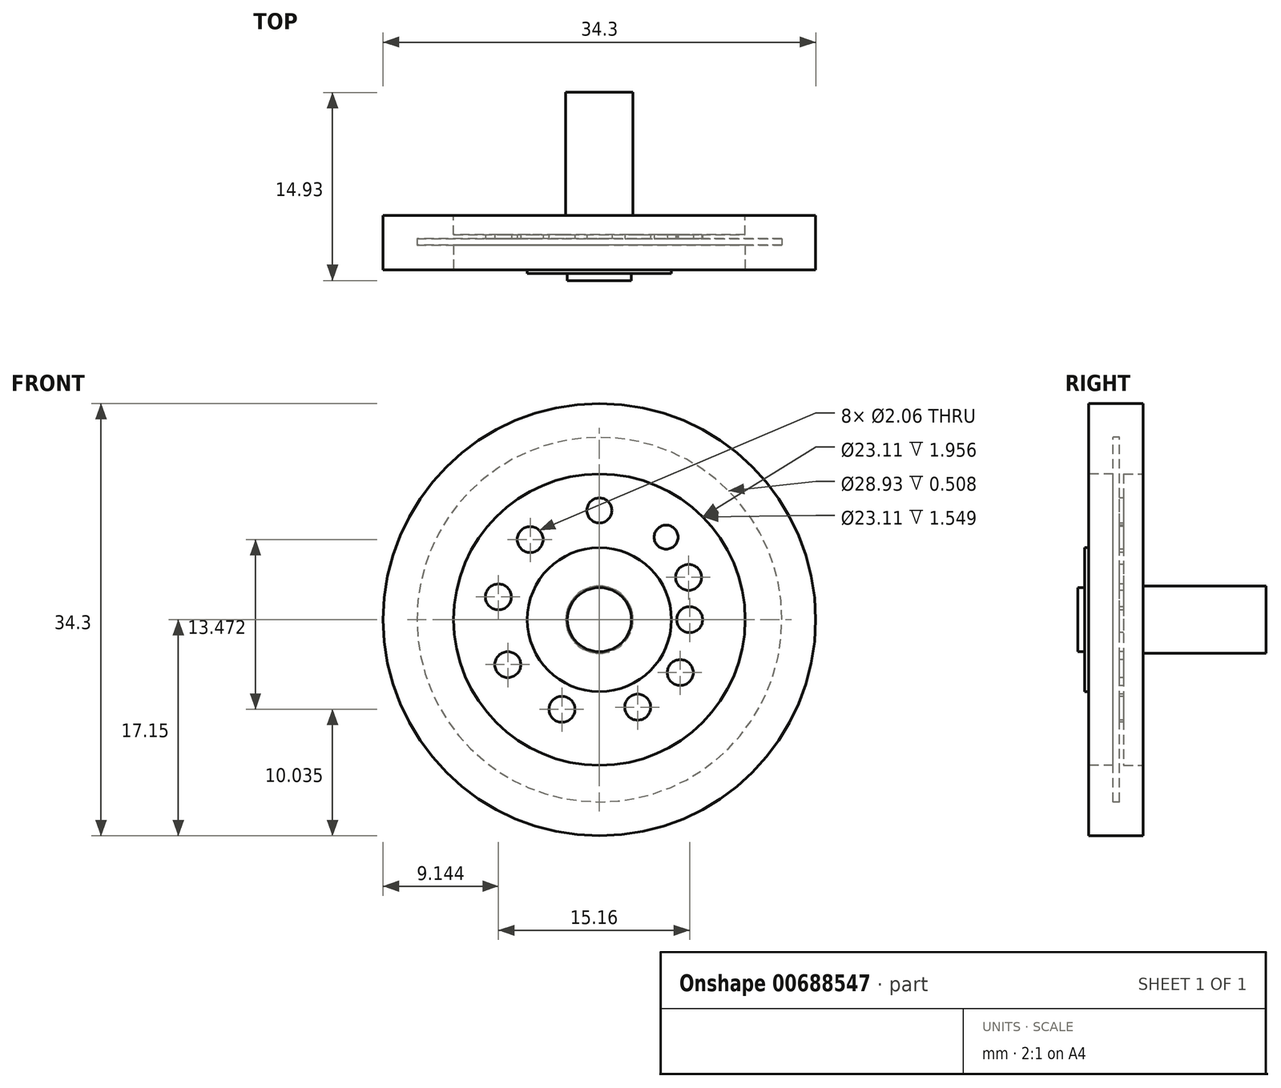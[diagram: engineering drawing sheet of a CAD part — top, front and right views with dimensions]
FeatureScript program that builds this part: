
annotation { "Feature Type Name" : "Feature", "Feature Type Description" : "" }
export const myFeature = defineFeature(function(context is Context, id is Id, definition is map)
    precondition{}
    {
        {
            var Q0;
            Q0=qCreatedBy(makeId("Front.planeOp"),FACE);
            var sketch = newSketch(context, id + "F0", { "sketchPlane" : qUnion([Q0])});
            skCircle(sketch, "E0", {"center": v(0, 0) * mm, "radius": 17.15 * mm});
            skSolve(sketch);
        }
        {
            var Q0;
            Q0=makeQuery(id+"F0.imprint","IMPRINT",FACE,{"disambiguationData":[TD([[makeQuery(id+"F0.imprint","IMPRINT",EDGE,{"derivedFrom":sQuery(id+"F0.wireOp",EDGE,"E0")}),1.0]])]});
            extrude(context, id + "F1", {"entities" : qUnion([Q0]), "depth" : 4.32 * mm, "offsetDistance" : 25.4 * mm});
        }
        {
            var Q0;
            Q0=qCreatedBy(makeId("Front.planeOp"),FACE);
            var sketch = newSketch(context, id + "F2", { "sketchPlane" : qUnion([Q0])});
            skCircle(sketch, "E1", {"center": v(0, 0) * mm, "radius": 2.67 * mm});
            skSolve(sketch);
        }
        {
            var Q0;
            Q0=makeQuery(id+"F2.imprint","IMPRINT",FACE,{"disambiguationData":[TD([[makeQuery(id+"F2.imprint","IMPRINT",EDGE,{"derivedFrom":sQuery(id+"F2.wireOp",EDGE,"E1")}),1.0]])]});
            extrude(context, id + "F3", {"entities" : qUnion([Q0]), "operationType" : NewBodyOperationType.ADD, "oppositeDirection" : true, "depth" : 9.75 * mm, "offsetDistance" : 25.4 * mm});
        }
        {
            var Q0;
            Q0=makeQuery(id+"F1.opExtrude","CAP_FACE",FACE,{"disambiguationData":[OSD([sQuery(id+"F0.wireOp",EDGE,"E0")])],"isStart":false});
            var sketch = newSketch(context, id + "F4", { "sketchPlane" : qUnion([Q0])});
            skCircle(sketch, "E2", {"center": v(0, 0) * mm, "radius": 2.54 * mm});
            skSolve(sketch);
        }
        {
            var Q0;
            Q0 = qSketchRegion(id + "F4", true);
            extrude(context, id + "F5", {"entities" : qUnion([Q0]), "operationType" : NewBodyOperationType.ADD, "depth" : 0.86 * mm, "offsetDistance" : 25.4 * mm});
        }
        {
            var Q0;
            Q0=makeQuery(id+"F1.opExtrude","CAP_FACE",FACE,{"disambiguationData":[OSD([sQuery(id+"F0.wireOp",EDGE,"E0")])],"isStart":false});
            var sketch = newSketch(context, id + "F6", { "sketchPlane" : qUnion([Q0])});
            skCircle(sketch, "E3", {"center": v(0, 0) * mm, "radius": 5.72 * mm});
            skSolve(sketch);
        }
        {
            var Q0;
            Q0 = qSketchRegion(id + "F6", true);
            extrude(context, id + "F7", {"entities" : qUnion([Q0]), "operationType" : NewBodyOperationType.ADD, "depth" : 0.3 * mm, "offsetDistance" : 25.4 * mm});
        }
        {
            var Q0;
            Q0=makeQuery(id+"F1.opExtrude","CAP_FACE",FACE,{"disambiguationData":[OSD([sQuery(id+"F0.wireOp",EDGE,"E0")])],"isStart":false});
            var sketch = newSketch(context, id + "F8", { "sketchPlane" : qUnion([Q0])});
            skCircle(sketch, "E4", {"center": v(0, 0) * mm, "radius": 11.56 * mm});
            skSolve(sketch);
        }
        {
            var Q0;
            Q0 = qSketchRegion(id + "F8", true);
            extrude(context, id + "F9", {"entities" : qUnion([Q0]), "operationType" : NewBodyOperationType.REMOVE, "oppositeDirection" : true, "depth" : 1.96 * mm, "offsetDistance" : 25.4 * mm});
        }
        {
            var Q0;
            Q0=makeQuery(id+"F9.boolean.opBoolean","COPY",FACE,{"derivedFrom":makeQuery(id+"F9.opExtrude","CAP_FACE",FACE,{"disambiguationData":[OSD([sQuery(id+"F8.wireOp",EDGE,"E4")])],"isStart":false})});
            var sketch = newSketch(context, id + "F10", { "sketchPlane" : qUnion([Q0])});
            skCircle(sketch, "E5", {"center": v(0, 0) * mm, "radius": 14.46 * mm});
            skSolve(sketch);
        }
        {
            var Q0;
            Q0 = qSketchRegion(id + "F10", true);
            extrude(context, id + "F11", {"entities" : qUnion([Q0]), "operationType" : NewBodyOperationType.REMOVE, "oppositeDirection" : true, "depth" : 0.5 * mm, "offsetDistance" : 25.4 * mm});
        }
        {
            var Q0;
            Q0=makeQuery(id+"F1.opExtrude","CAP_FACE",FACE,{"disambiguationData":[OSD([sQuery(id+"F0.wireOp",EDGE,"E0")])],"isStart":false});
            var sketch = newSketch(context, id + "F12", { "sketchPlane" : qUnion([Q0])});
            skCircle(sketch, "E6", {"center": v(0, 8.66) * mm, "radius": 1 * mm});
            skSolve(sketch);
        }
        {
            var Q0;
            Q0 = qSketchRegion(id + "F12", true);
            extrude(context, id + "F13", {"entities" : qUnion([Q0]), "operationType" : NewBodyOperationType.REMOVE, "oppositeDirection" : true, "depth" : 35.4 * mm, "offsetDistance" : 25.4 * mm});
        }
        {
            var Q0;
            Q0=makeQuery(id+"F1.opExtrude","CAP_FACE",FACE,{"disambiguationData":[OSD([sQuery(id+"F0.wireOp",EDGE,"E0")])],"isStart":true});
            var sketch = newSketch(context, id + "F14", { "sketchPlane" : qUnion([Q0])});
            skCircle(sketch, "E7", {"center": v(0, 0) * mm, "radius": 11.56 * mm});
            skSolve(sketch);
        }
        {
            var Q0;
            Q0 = qSketchRegion(id + "F14", true);
            extrude(context, id + "F15", {"entities" : qUnion([Q0]), "operationType" : NewBodyOperationType.REMOVE, "oppositeDirection" : true, "depth" : 1.55 * mm, "offsetDistance" : 25.4 * mm});
        }
        {
            var Q0;
            Q0=makeQuery(id+"F1.opExtrude","CAP_FACE",FACE,{"disambiguationData":[OSD([sQuery(id+"F0.wireOp",EDGE,"E0")])],"isStart":true});
            var sketch = newSketch(context, id + "F16", { "sketchPlane" : qUnion([Q0])});
            skCircle(sketch, "E8", {"center": v(0, 0) * mm, "radius": 14.74 * mm});
            skSolve(sketch);
        }
        {
            var Q0;
            Q0=sQuery(id+"F16.wireOp",EDGE,"E8");
            extrude(context, id + "F17", {"bodyType" : ToolBodyType.SURFACE, "surfaceEntities" : qUnion([Q0]), "oppositeDirection" : true, "depth" : 4.32 * mm, "offsetDistance" : 25.4 * mm});
        }
        {
            var Q0;
            Q0=makeQuery(id+"F1.opExtrude","CAP_FACE",FACE,{"disambiguationData":[OSD([sQuery(id+"F0.wireOp",EDGE,"E0")])],"isStart":false});
            var sketch = newSketch(context, id + "F18", { "sketchPlane" : qUnion([Q0])});
            skCircle(sketch, "E9", {"center": v(5.29, 6.54) * mm, "radius": 0.95 * mm});
            skSolve(sketch);
        }
        {
            var Q0;
            Q0=makeQuery(id+"F18.imprint","IMPRINT",FACE,{"disambiguationData":[TD([[makeQuery(id+"F18.imprint","IMPRINT",EDGE,{"derivedFrom":sQuery(id+"F18.wireOp",EDGE,"E9")}),1.0]])]});
            extrude(context, id + "F19", {"entities" : qUnion([Q0]), "operationType" : NewBodyOperationType.REMOVE, "oppositeDirection" : true, "depth" : 25.4 * mm, "offsetDistance" : 25.4 * mm});
        }
        {
            var Q0;
            Q0=makeQuery(id+"F1.opExtrude","CAP_FACE",FACE,{"disambiguationData":[OSD([sQuery(id+"F0.wireOp",EDGE,"E0")])],"isStart":false});
            var sketch = newSketch(context, id + "F20", { "sketchPlane" : qUnion([Q0])});
            skCircle(sketch, "E10", {"center": v(-5.72, 6.83) * mm, "radius": 1.03 * mm});
            skCircle(sketch, "E11", {"center": v(-8, 1.8) * mm, "radius": 1.03 * mm});
            skCircle(sketch, "E12", {"center": v(-7.26, -3.57) * mm, "radius": 1.03 * mm});
            skCircle(sketch, "E13", {"center": v(-2.97, -7.12) * mm, "radius": 1.03 * mm});
            skCircle(sketch, "E14", {"center": v(3.04, -6.94) * mm, "radius": 1.03 * mm});
            skCircle(sketch, "E15", {"center": v(6.41, -4.2) * mm, "radius": 1.03 * mm});
            skCircle(sketch, "E16", {"center": v(7.15, 0) * mm, "radius": 1.03 * mm});
            skCircle(sketch, "E17", {"center": v(7.07, 3.35) * mm, "radius": 1.03 * mm});
            skSolve(sketch);
        }
        {
            var Q0;
            Q0=makeQuery(id+"F20.imprint","IMPRINT",FACE,{"disambiguationData":[TD([[makeQuery(id+"F20.imprint","IMPRINT",EDGE,{"derivedFrom":sQuery(id+"F20.wireOp",EDGE,"E11")}),1.0]])]});
            var Q1;
            Q1=makeQuery(id+"F20.imprint","IMPRINT",FACE,{"disambiguationData":[TD([[makeQuery(id+"F20.imprint","IMPRINT",EDGE,{"derivedFrom":sQuery(id+"F20.wireOp",EDGE,"E12")}),1.0]])]});
            var Q2;
            Q2=makeQuery(id+"F20.imprint","IMPRINT",FACE,{"disambiguationData":[TD([[makeQuery(id+"F20.imprint","IMPRINT",EDGE,{"derivedFrom":sQuery(id+"F20.wireOp",EDGE,"E13")}),1.0]])]});
            var Q3;
            Q3=makeQuery(id+"F20.imprint","IMPRINT",FACE,{"disambiguationData":[TD([[makeQuery(id+"F20.imprint","IMPRINT",EDGE,{"derivedFrom":sQuery(id+"F20.wireOp",EDGE,"E14")}),1.0]])]});
            var Q4;
            Q4=makeQuery(id+"F20.imprint","IMPRINT",FACE,{"disambiguationData":[TD([[makeQuery(id+"F20.imprint","IMPRINT",EDGE,{"derivedFrom":sQuery(id+"F20.wireOp",EDGE,"E15")}),1.0]])]});
            var Q5;
            Q5=makeQuery(id+"F20.imprint","IMPRINT",FACE,{"disambiguationData":[TD([[makeQuery(id+"F20.imprint","IMPRINT",EDGE,{"derivedFrom":sQuery(id+"F20.wireOp",EDGE,"E16")}),1.0]])]});
            var Q6;
            Q6=makeQuery(id+"F20.imprint","IMPRINT",FACE,{"disambiguationData":[TD([[makeQuery(id+"F20.imprint","IMPRINT",EDGE,{"derivedFrom":sQuery(id+"F20.wireOp",EDGE,"E17")}),1.0]])]});
            extrude(context, id + "F21", {"entities" : qUnion([Q0, Q1, Q2, Q3, Q4, Q5, Q6]), "operationType" : NewBodyOperationType.REMOVE, "oppositeDirection" : true, "depth" : 25.4 * mm, "offsetDistance" : 25.4 * mm});
        }
        {
            var Q0;
            Q0=makeQuery(id+"F1.opExtrude","CAP_FACE",FACE,{"disambiguationData":[OSD([sQuery(id+"F0.wireOp",EDGE,"E0")])],"isStart":false});
            var sketch = newSketch(context, id + "F22", { "sketchPlane" : qUnion([Q0])});
            skCircle(sketch, "E18", {"center": v(-5.49, 6.36) * mm, "radius": 1.03 * mm});
            skSolve(sketch);
        }
        {
            var Q0;
            Q0 = qSketchRegion(id + "F22", true);
            extrude(context, id + "F23", {"entities" : qUnion([Q0]), "operationType" : NewBodyOperationType.REMOVE, "oppositeDirection" : true, "depth" : 25.4 * mm, "offsetDistance" : 25.4 * mm});
        }
    });
